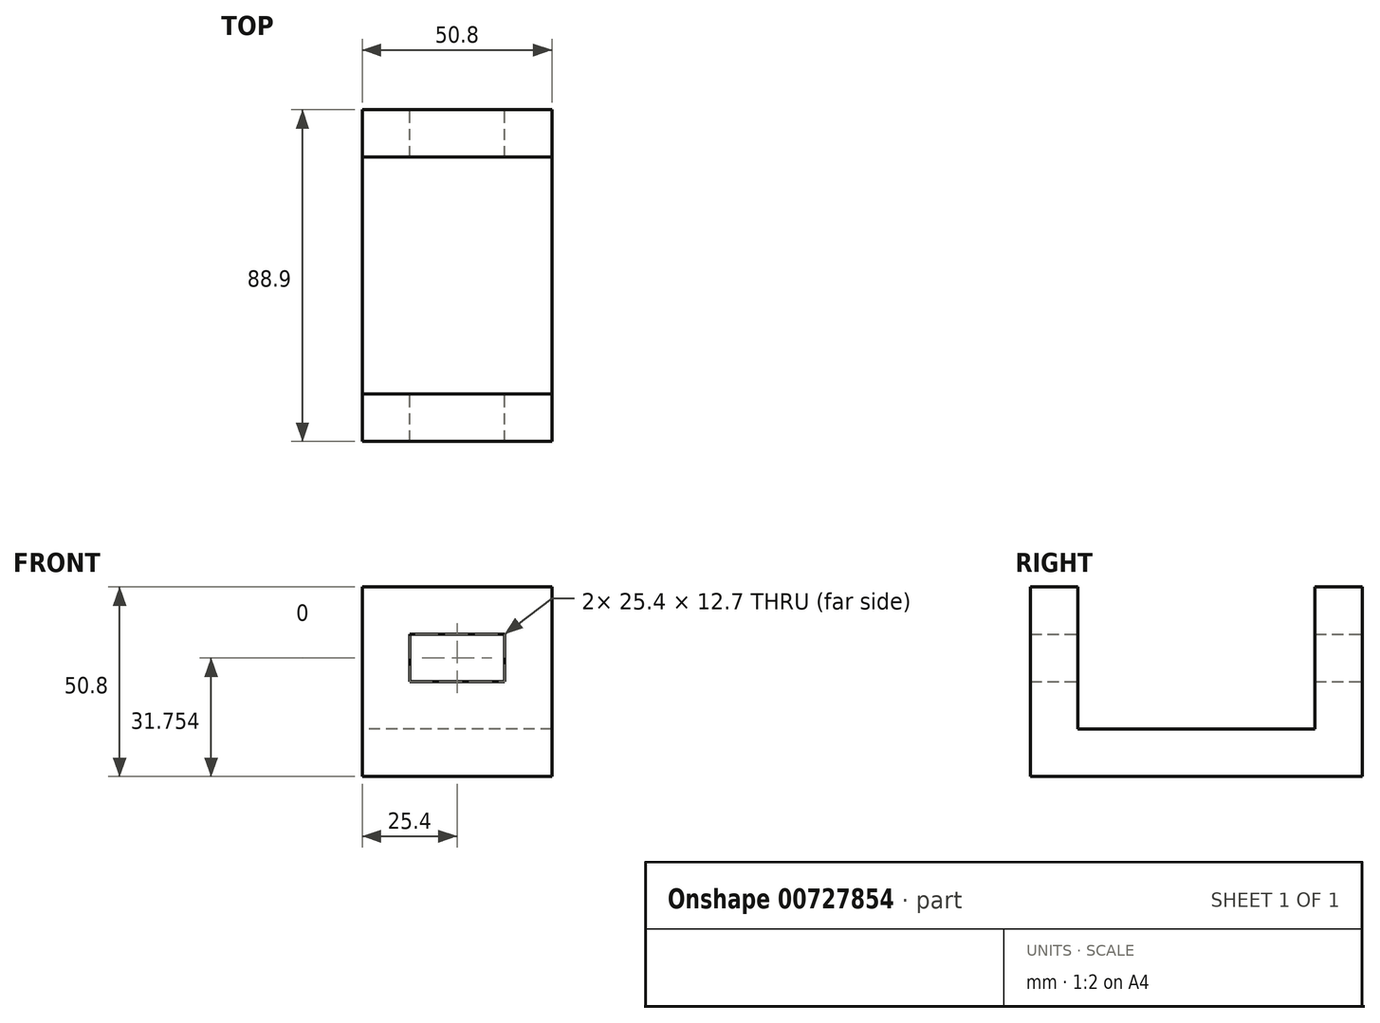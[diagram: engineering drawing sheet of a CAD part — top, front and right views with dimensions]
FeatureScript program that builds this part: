
annotation { "Feature Type Name" : "Feature", "Feature Type Description" : "" }
export const myFeature = defineFeature(function(context is Context, id is Id, definition is map)
    precondition{}
    {
        {
            var Q0;
            Q0=qCreatedBy(makeId("Right.planeOp"),FACE);
            var sketch = newSketch(context, id + "F0", { "sketchPlane" : qUnion([Q0])});
            skLineSegment(sketch, "E0", {"start": v(-48.48, 23.57) * mm, "end": v(-48.48, -27.23) * mm});
            skLineSegment(sketch, "E1", {"start": v(-48.48, -27.23) * mm, "end": v(40.42, -27.23) * mm});
            skLineSegment(sketch, "E2", {"start": v(40.42, -27.23) * mm, "end": v(40.42, 23.57) * mm});
            skLineSegment(sketch, "E3", {"start": v(-48.48, 23.57) * mm, "end": v(-35.78, 23.57) * mm});
            skLineSegment(sketch, "E4", {"start": v(-35.78, 23.57) * mm, "end": v(-35.78, -14.53) * mm});
            skLineSegment(sketch, "E5", {"start": v(-35.78, -14.53) * mm, "end": v(27.72, -14.53) * mm});
            skLineSegment(sketch, "E6", {"start": v(27.72, -14.53) * mm, "end": v(27.72, 23.57) * mm});
            skLineSegment(sketch, "E7", {"start": v(27.72, 23.57) * mm, "end": v(40.42, 23.57) * mm});
            skSolve(sketch);
        }
        {
            var Q0;
            Q0=makeQuery(id+"F0.imprint","IMPRINT",FACE,{"disambiguationData":[TD([[makeQuery(id+"F0.imprint","IMPRINT",EDGE,{"derivedFrom":sQuery(id+"F0.wireOp",EDGE,"E0")}),1.0]])]});
            extrude(context, id + "F1", {"entities" : qUnion([Q0]), "depth" : 50.8 * mm, "offsetDistance" : 25.4 * mm});
        }
        {
            var Q0;
            Q0=makeQuery(id+"F1.opExtrude","SWEPT_FACE",FACE,{"disambiguationData":[OSD([sQuery(id+"F0.wireOp",EDGE,"E2")])]});
            var sketch = newSketch(context, id + "F2", { "sketchPlane" : qUnion([Q0])});
            skLineSegment(sketch, "E8.bottom", {"start": v(-38.1, 10.87) * mm, "end": v(-12.7, 10.87) * mm});
            skLineSegment(sketch, "E8.top", {"start": v(-38.1, -1.83) * mm, "end": v(-12.7, -1.83) * mm});
            skLineSegment(sketch, "E8.left", {"start": v(-38.1, 10.87) * mm, "end": v(-38.1, -1.83) * mm});
            skLineSegment(sketch, "E8.right", {"start": v(-12.7, 10.87) * mm, "end": v(-12.7, -1.83) * mm});
            skSolve(sketch);
        }
        {
            var Q0;
            Q0=makeQuery(id+"F2.imprint","IMPRINT",FACE,{"disambiguationData":[TD([[makeQuery(id+"F2.imprint","IMPRINT",EDGE,{"derivedFrom":sQuery(id+"F2.wireOp",EDGE,"E8.bottom")}),-1.0]])]});
            extrude(context, id + "F3", {"entities" : qUnion([Q0]), "operationType" : NewBodyOperationType.REMOVE, "oppositeDirection" : true, "depth" : 88.9 * mm, "offsetDistance" : 25.4 * mm});
        }
    });
